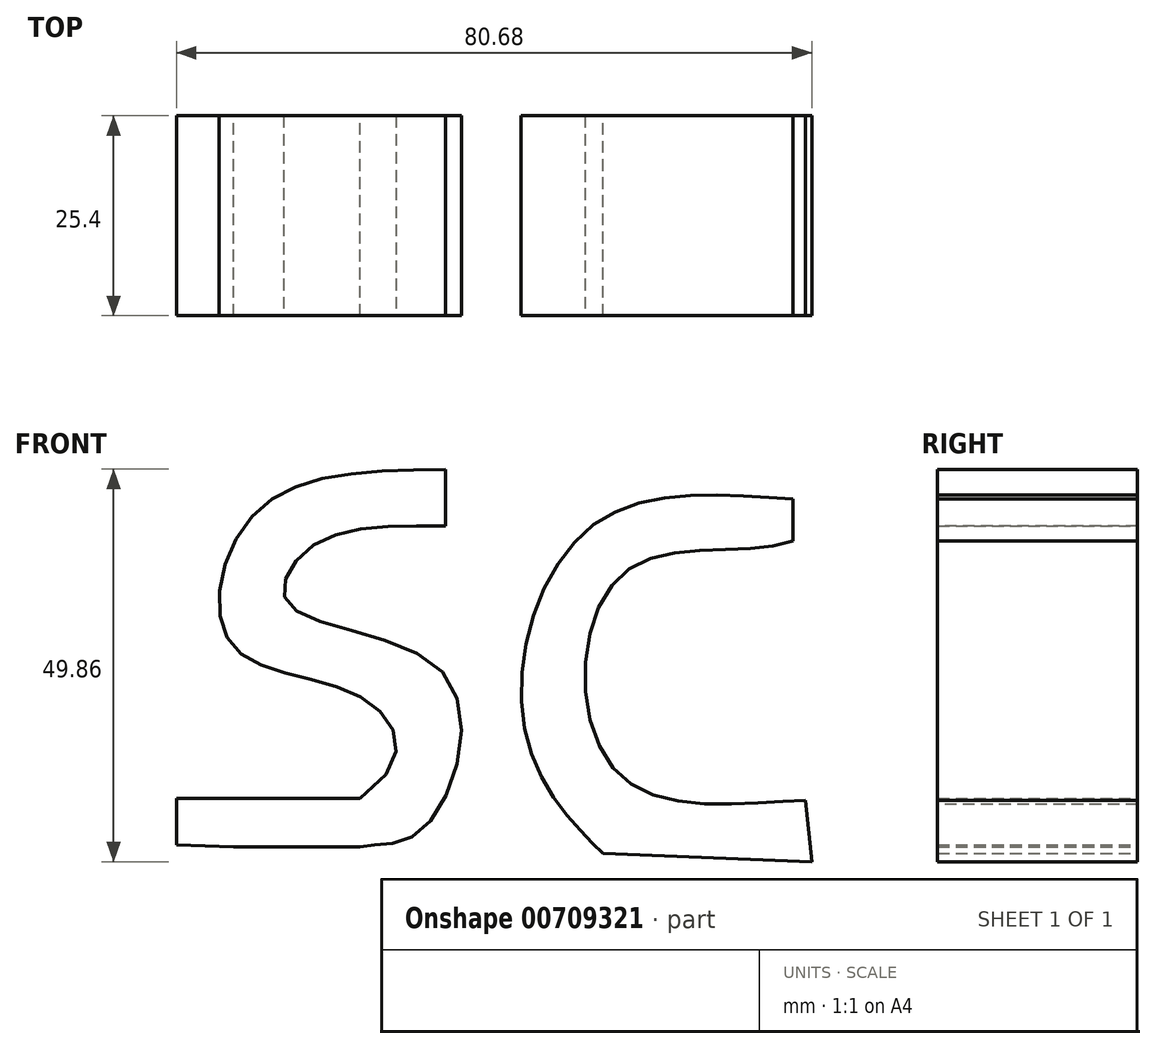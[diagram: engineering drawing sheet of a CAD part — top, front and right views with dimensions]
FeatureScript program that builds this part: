
annotation { "Feature Type Name" : "Feature", "Feature Type Description" : "" }
export const myFeature = defineFeature(function(context is Context, id is Id, definition is map)
    precondition{}
    {
        {
            var Q0;
            Q0=qCreatedBy(makeId("Front.planeOp"),FACE);
            var sketch = newSketch(context, id + "F0", { "sketchPlane" : qUnion([Q0])});
            skFitSpline(sketch, "E0", {"points": [v(0, 46.37) * mm, v(-16.75, 43.96) * mm, v(-19.97, 36.45) * mm, v(0, 27.34) * mm, v(-3.35, 7.5) * mm, v(-10.86, 5.63) * mm], "startDerivative": vector(-85.15, 0.87) * mm, "endDerivative": vector(-34.17, -11.09) * mm});
            skLineSegment(sketch, "E1", {"start": v(-10.86, 5.63) * mm, "end": v(-26.94, 5.63) * mm});
            skLineSegment(sketch, "E2", {"start": v(-26.94, 11.8) * mm, "end": v(-10.86, 11.8) * mm});
            skFitSpline(sketch, "E3", {"points": [v(-10.86, 11.8) * mm, v(-10.32, 24.4) * mm, v(-27.2, 31.36) * mm, v(-23.99, 48.25) * mm, v(0, 53.6) * mm], "startDerivative": vector(100.97, 69.9) * mm, "endDerivative": vector(93.81, 2.46) * mm});
            skLineSegment(sketch, "E4", {"start": v(0, 46.37) * mm, "end": v(0, 53.6) * mm});
            skLineSegment(sketch, "E5", {"start": v(-26.94, 11.8) * mm, "end": v(-34.18, 11.8) * mm});
            skLineSegment(sketch, "E6", {"start": v(-34.18, 11.8) * mm, "end": v(-34.18, 5.9) * mm});
            skLineSegment(sketch, "E7", {"start": v(-34.18, 5.9) * mm, "end": v(-26.94, 5.63) * mm});
            skSolve(sketch);
        }
        {
            var Q0;
            Q0=makeQuery(id+"F0.imprint","IMPRINT",FACE,{"disambiguationData":[TD([[makeQuery(id+"F0.imprint","IMPRINT",EDGE,{"derivedFrom":sQuery(id+"F0.wireOp",EDGE,"E0")}),-1.0]])]});
            extrude(context, id + "F1", {"entities" : qUnion([Q0]), "depth" : 25.4 * mm, "offsetDistance" : 25.4 * mm});
        }
        {
            var Q0;
            Q0=qCreatedBy(makeId("Front.planeOp"),FACE);
            var sketch = newSketch(context, id + "F2", { "sketchPlane" : qUnion([Q0])});
            skFitSpline(sketch, "E8", {"points": [v(44.1, 44.5) * mm, v(22.38, 40.2) * mm, v(21.85, 15.01) * mm, v(45.7, 11.53) * mm], "startDerivative": vector(-51.3, -20.83) * mm, "endDerivative": vector(60.22, 0.75) * mm});
            skLineSegment(sketch, "E9", {"start": v(44.1, 44.5) * mm, "end": v(44.1, 49.86) * mm});
            skFitSpline(sketch, "E10", {"points": [v(44.1, 49.86) * mm, v(18.9, 46.64) * mm, v(10.32, 19.3) * mm, v(19.97, 4.82) * mm], "startDerivative": vector(-67.47, 3.52) * mm, "endDerivative": vector(25.64, -25.4) * mm});
            skLineSegment(sketch, "E11", {"start": v(19.97, 4.82) * mm, "end": v(46.5, 3.75) * mm});
            skLineSegment(sketch, "E12", {"start": v(46.5, 3.75) * mm, "end": v(45.7, 11.53) * mm});
            skSolve(sketch);
        }
        {
            var Q0;
            Q0 = qSketchRegion(id + "F2", true);
            extrude(context, id + "F3", {"entities" : qUnion([Q0]), "depth" : 25.4 * mm, "offsetDistance" : 25.4 * mm});
        }
    });
